# Revit family: Urinal-Wall_Mount-KOHLER-SPAN-K-26474T-1
name_source: partatom
category: Plumbing Fixtures
units: mm (PartAtom-declared; Revit-internal decimal feet)

## family parameters
Cut with Voids When Loaded = No
Host = Face
OmniClass Number = 23.31.21.00
OmniClass Title = Urinals
Part Type = Normal
Room Calculation Point = No
Round Connector Dimension = Use Diameter
Shared = No

## types (2) — shared parameters
ADA Compliant = No
Assembly Code = D2010200
CW Connection = Yes
Cold Water Inlet = Cold Water Inlet
Date Modified = 12/203/2024
Default Elevation = 0"
Drain Included = No
Finish = Kohler-Vitreous_China-0-White
Flow Rate = 0 GPM
HW Connection = No
Height = 24 1/4"
Hot Water Inlet = Hot Water Inlet
Length = 14 5/16"
Manufacturer = Kohler Co.
Master Format 2014 = 22 41 13.16
Master Format 2014 Name = Residential Urinals
Material = Vitreous China
Pressure = 0.00 psi
Product Name = SPAN
URL = http://www.kohler.com.cn
Vent Connection = No
Waste Connection = Yes
Waste Water Outlet = Waste Water Outlet
WaterSense Certified = No
Width = 12 13/16"

## per-type parameters (varying)
| type | Description | Flush Rate- GPF | Flush Rate- LPF | Model | Product Documentation Link | Product Page URL | Type |
| 0.5 GPF, 0-White | Square Urinal,Rear Spud , 0.5 GPF | 0.66 GPF | 0.5LPF | K-26474T-ER-0 | https://files.kohler.com.cn | https://www.kohler.com.cn | 1 |
| 2.5 GPF, 0-White | Square Urinal,Rear Spud , 2.5 GPF | 0.132 GPF | 2.5LPF | K-26474T-2ER-0 |  |  | 2 |

## geometry (parser evidence)
native form markers: Sweep x5
no freeform markers — native parametric forms only
